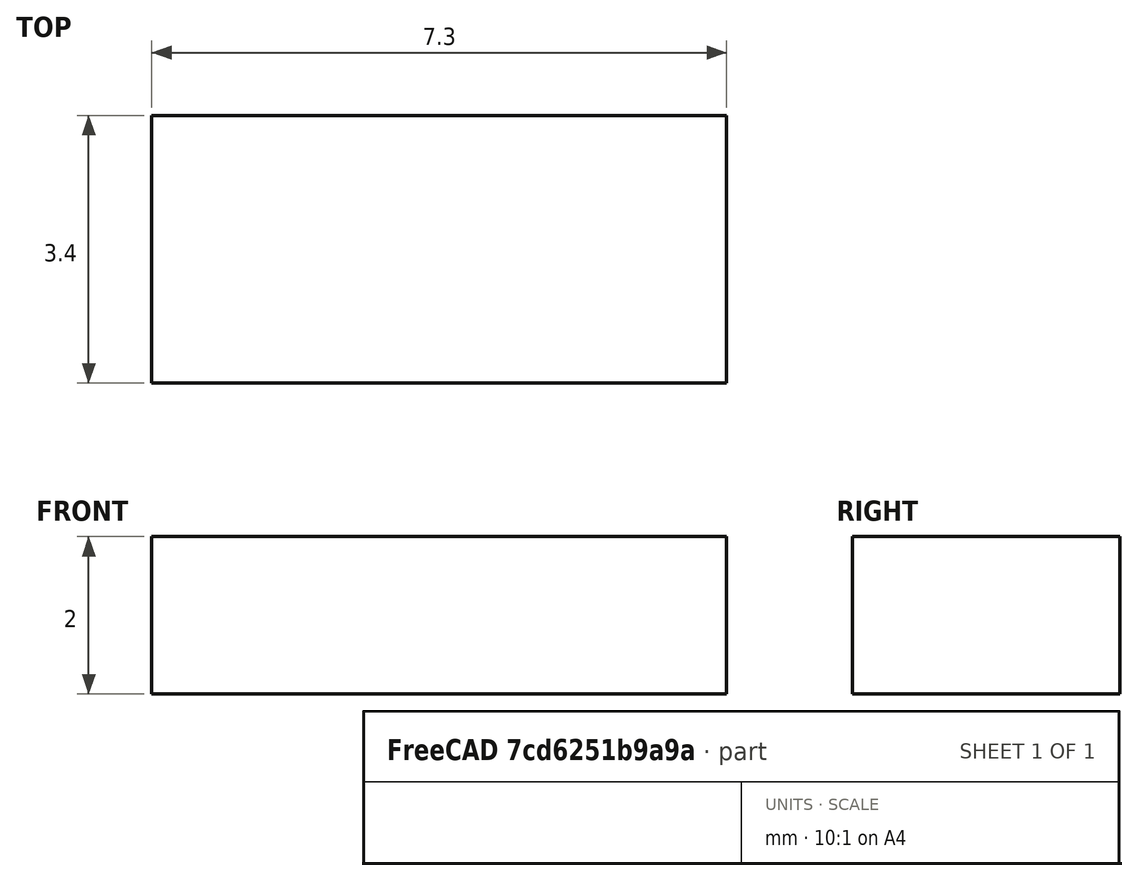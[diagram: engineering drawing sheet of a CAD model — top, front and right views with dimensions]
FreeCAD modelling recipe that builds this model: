
FCSTD DOCUMENT  (FreeCAD 0.21R33668 +26 (Git))
Label: OS_Qwiic_Opening_cutaway
License: All rights reserved
LicenseURL: http://en.wikipedia.org/wiki/All_rights_reserved
objects: Sketcher::SketchObject×1, PartDesign::Pad×1, PartDesign::Body×1
note: 4 computed .brp shape members not serialized (recipe doc carries the construction recipe); baked Part::Feature solids carry a one-line shape summary decoded from their .brp

FEATURE [Sketcher::SketchObject] Sketch
  FullyConstrained = true
  MapMode = 5
  Support = -> [XY_Plane]
  sketch-geometry (5):
    g0: LineSegment StartX=3.65 StartY=0 StartZ=0 EndX=3.65 EndY=3.4 EndZ=0
    g1: LineSegment StartX=3.65 StartY=3.4 StartZ=0 EndX=-3.65 EndY=3.4 EndZ=0
    g2: LineSegment StartX=-3.65 StartY=3.4 StartZ=0 EndX=-3.65 EndY=0 EndZ=0
    g3: LineSegment StartX=-3.65 StartY=0 StartZ=0 EndX=3.65 EndY=0 EndZ=0
    g4: GeomPoint X=0 Y=0 Z=0
  constraints (12):
    c: Coincident(g0,g1)
    c: Coincident(g1,g2)
    c: Coincident(g2,g3)
    c: Coincident(g3,g0)
    c: Horizontal(g3)
    c: Vertical(g0)
    c: Vertical(g2)
    c: Coincident(g4,g-1)
    c: DistanceX(g1,g1) = 7.3
    c: DistanceY(g0,g0) = 3.4
    c: PointOnObject(g0,g-1)
    c: Symmetric(g0,g1,g-2)
FEATURE [PartDesign::Pad] Pad
  Direction = (0,0,1)
  Length = 2
  Length2 = 10
  Profile = -> Sketch
  ReferenceAxis = -> Sketch [N_Axis]
  Type = 0
FEATURE [PartDesign::Body] Body
  Group = -> [Sketch,Pad]
  Origin = -> Origin
  Tip = -> Pad
